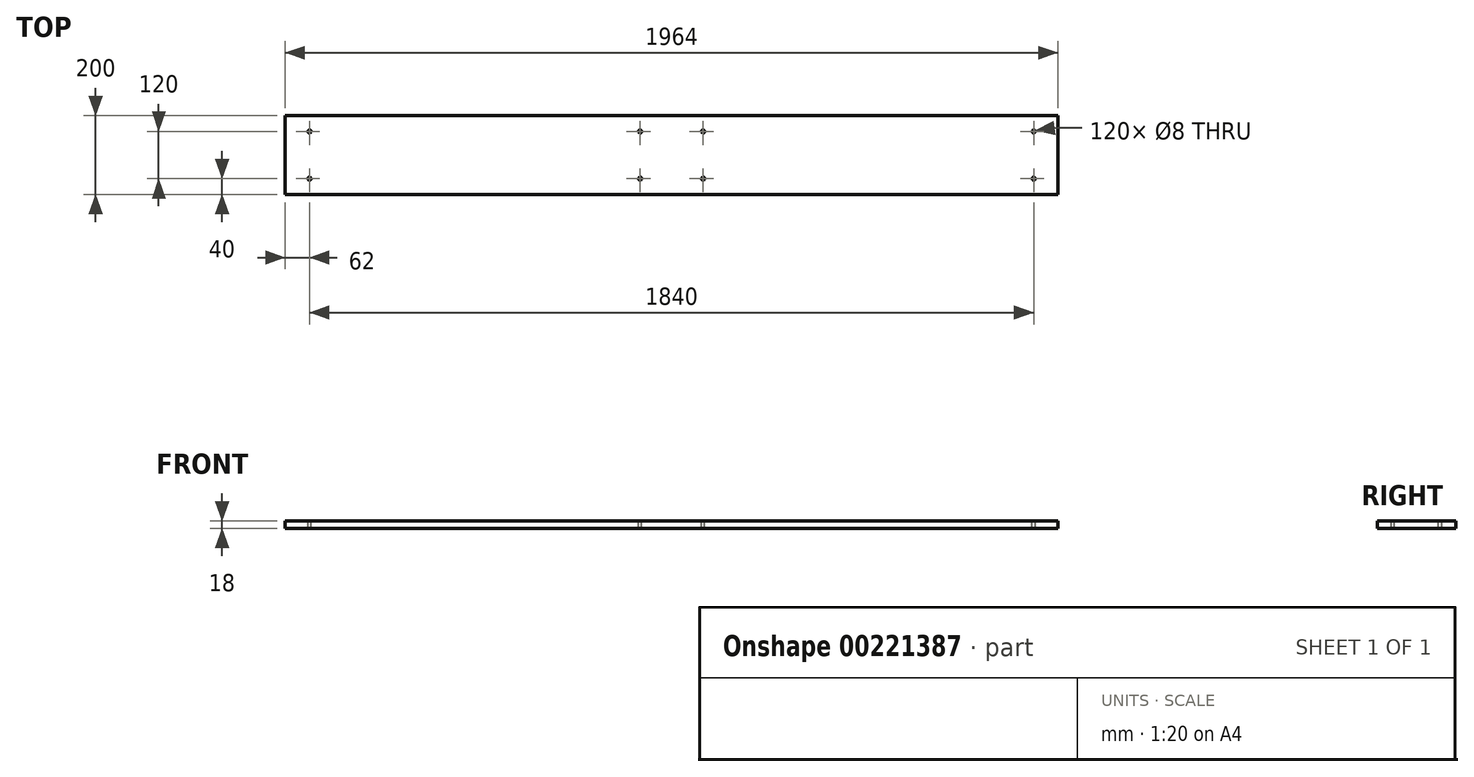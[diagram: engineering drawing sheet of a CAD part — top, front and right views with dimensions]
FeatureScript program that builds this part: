
annotation { "Feature Type Name" : "Feature", "Feature Type Description" : "" }
export const myFeature = defineFeature(function(context is Context, id is Id, definition is map)
    precondition{}
    {
        {
            var Q0;
            Q0=qCreatedBy(makeId("Top.planeOp"),FACE);
            var sketch = newSketch(context, id + "F0", { "sketchPlane" : qUnion([Q0])});
            skLineSegment(sketch, "E0.bottom", {"start": v(982, -100) * mm, "end": v(-982, -100) * mm});
            skLineSegment(sketch, "E0.top", {"start": v(982, 100) * mm, "end": v(-982, 100) * mm});
            skLineSegment(sketch, "E0.left", {"start": v(982, -100) * mm, "end": v(982, 100) * mm});
            skLineSegment(sketch, "E0.right", {"start": v(-982, -100) * mm, "end": v(-982, 100) * mm});
            skPoint(sketch, "E0.middle", {"position": v(0, 0) * mm});
            skSolve(sketch);
        }
        {
            var Q0;
            Q0=qSketchRegion(id+"F0",true);
            extrude(context, id + "F1", {"entities" : qUnion([Q0]), "depth" : 18 * mm});
        }
        {
            var Q0;
            Q0=makeQuery(id+"F1.opExtrude","CAP_FACE",FACE,{"disambiguationData":[OSD([sQuery(id+"F0.wireOp",EDGE,"E0.bottom"),sQuery(id+"F0.wireOp",EDGE,"E0.top"),sQuery(id+"F0.wireOp",EDGE,"E0.left"),sQuery(id+"F0.wireOp",EDGE,"E0.right")])],"isStart":false});
            var sketch = newSketch(context, id + "F2", { "sketchPlane" : qUnion([Q0])});
            skCircle(sketch, "E1", {"center": v(80, 60) * mm, "radius": 4 * mm});
            skCircle(sketch, "E2", {"center": v(-80, 60) * mm, "radius": 4 * mm});
            skCircle(sketch, "E3", {"center": v(80, -60) * mm, "radius": 4 * mm});
            skCircle(sketch, "E4", {"center": v(-80, -60) * mm, "radius": 4 * mm});
            skCircle(sketch, "E5", {"center": v(920, 60) * mm, "radius": 4 * mm});
            skCircle(sketch, "E6", {"center": v(920, -60) * mm, "radius": 4 * mm});
            skCircle(sketch, "E7", {"center": v(-920, 60) * mm, "radius": 4 * mm});
            skCircle(sketch, "E8", {"center": v(-920, -60) * mm, "radius": 4 * mm});
            skSolve(sketch);
        }
        {
            var Q0;
            Q0 = qSketchRegion(id + "F2", true);
            extrude(context, id + "F3", {"entities" : qUnion([Q0]), "operationType" : NewBodyOperationType.REMOVE, "oppositeDirection" : true, "depth" : 25 * mm});
        }
    });
